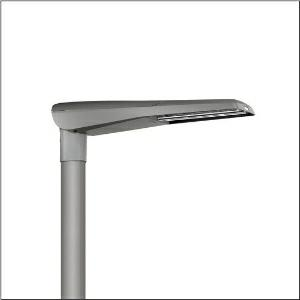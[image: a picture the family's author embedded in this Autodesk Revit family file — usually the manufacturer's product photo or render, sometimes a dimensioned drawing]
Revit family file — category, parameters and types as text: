
# Revit family: streetlight_sl_11_iq_mini___st1_0ab_5xc2nc1f08he_e776
name_source: partatom
category: Lighting Fixtures
units: mm (PartAtom-declared; Revit-internal decimal feet)

## family parameters
Cut with Voids When Loaded = No
Host = Face
Light Source = No
Part Type = Normal
Room Calculation Point = No
Round Connector Dimension = Use Diameter
Shared = No

## types (1)
- --- (1 x LED, 5460 lm, 63.6 W, 2200K)
    Apparent Load = 64 VA
    CIE Flux Codes = 29 63 95 100 100
    Color Rendering = 70
    Color Temperature = 2200K
    Default Elevation = 1800 mm
    Description = Streetlight SL 11 iQ mini, mast luminaire, primary light control with 3 zone facetted reflector, of plastic, silver coated, highly specular, primary optical cover: cover, of PMMA, transparent, light distribution: ST1.0aB, light emission: direct distribution, primary light characteristic: asymmetric, installation type: post-top, side-entry, lamps: LED, High Power LED, rated values: 6.670lm | 62,2W | 107,2lm/W (begin service life); end service life: 6.670lm | 65,6W; at 50% lumin. flux: 3.335lm | 29,4W | 113,4lm/W, colour temperature: 2200/2700/3000/4000K, colour rendering: CRI > 70, light colour: 722/727/730/740, light setting 1 begin service life: 100% | 6.670lm | 62,2W | 107,2lm/W | 3.000K, light setting 1 end service life: 65,6W, further light settings possible, control: Street-Remote, Auto-Match, Temp-Guard, Lumen-Switch, Night-Set, Smart-Wire, Light-Fading, Desk-Remote (wireless, voltage-free reading and setting of iQ features in the workshop via application-optimized NFC function/RFID function), optimised constant luminous flux control (CLO 2.0), with cable H07RN-F 3x 1.5mm², mains connection: 230..240V, AC, 50/60Hz, connection cable pre-assembled, cable length: 8,5m, luminaire housing, of diecast aluminium, powder-coated, SITECO metallic grey (DB 702S), please order mast flange separately, inclination adjustable without tools: 0°, 5°, 10°, 15° (post-top) | 0°, -5°, -10°, -15° (side-entry), sealing non-destructively replaceable, multi-level sealing system, length: 736mm, width: 174mm, height: 116mm, mast flange for spigot size: 42mm (side-entry): 5XC10008XM4, 60/48mm (side-entry/post-top): 5XC10108XM2, 76/60mm (side-entry/post-top): 5XC10108XM1, equipment: Power, protection rating (complete): IP66, insulation class (complete): insulation class II (safety insulation), certification: CE, ENEC, ENEC+, VDE, impact resistance: IK10, permissible operating ambient temperature for outdoor applications: -25..+50°C, standard-compliant lighting for roads and squares, Environmental Product Declaration (EPD) tested and certified by an independent institute, packaging unit: 1 piece

Light Distribution: ST1.0aB
    Height = 116 mm
    Lamp = 1 x LED
    Lamp Light Flux = 5460 lm
    Lamp Power = 63.6 W
    Lamp count = 1
    Length = 736 mm
    Luminous efficacy = 86 lm/W
    Manufacturer = Siteco
    ModVariant = No
    Model = 5XC2NC1F08HE
    Number of Poles = 1
    OnlyDefault = Yes
    Power Factor = 1
    Product Name = Streetlight SL 11 iQ mini | ST1.0aB
    Product group = mast luminaire | pylon top
    ProductGroupID = 6100
    Protection Class = Protection class II
    Protection Degree = IP 66
    RLX_Detail_Level = 1
    RLX_Emergency_Light_Flux = 0 lm
    RLX_Emergency_Type = 0
    RLX_Emergency_Type_DB = No
    RlxData = <blob elided: 53053 chars, md5=4fc1491d>
    Socket = socket
    Standby Power = 0 W
    System Light Flux = 5460 lm
    System Power = 64 W
    Type Comments = individual setting: luminous flux: 100 % | dim-lin: 254 | 866 mA
    Type Image = l_1003508.jpg
    URL = http://relux.com
    VarID = @adj_020959
    Voltage = 0 V
    Weight = 0.00 kg
    Width = 174 mm

## geometry (parser evidence)
native form markers: Blend x4, Sweep x10
no freeform markers — native parametric forms only
